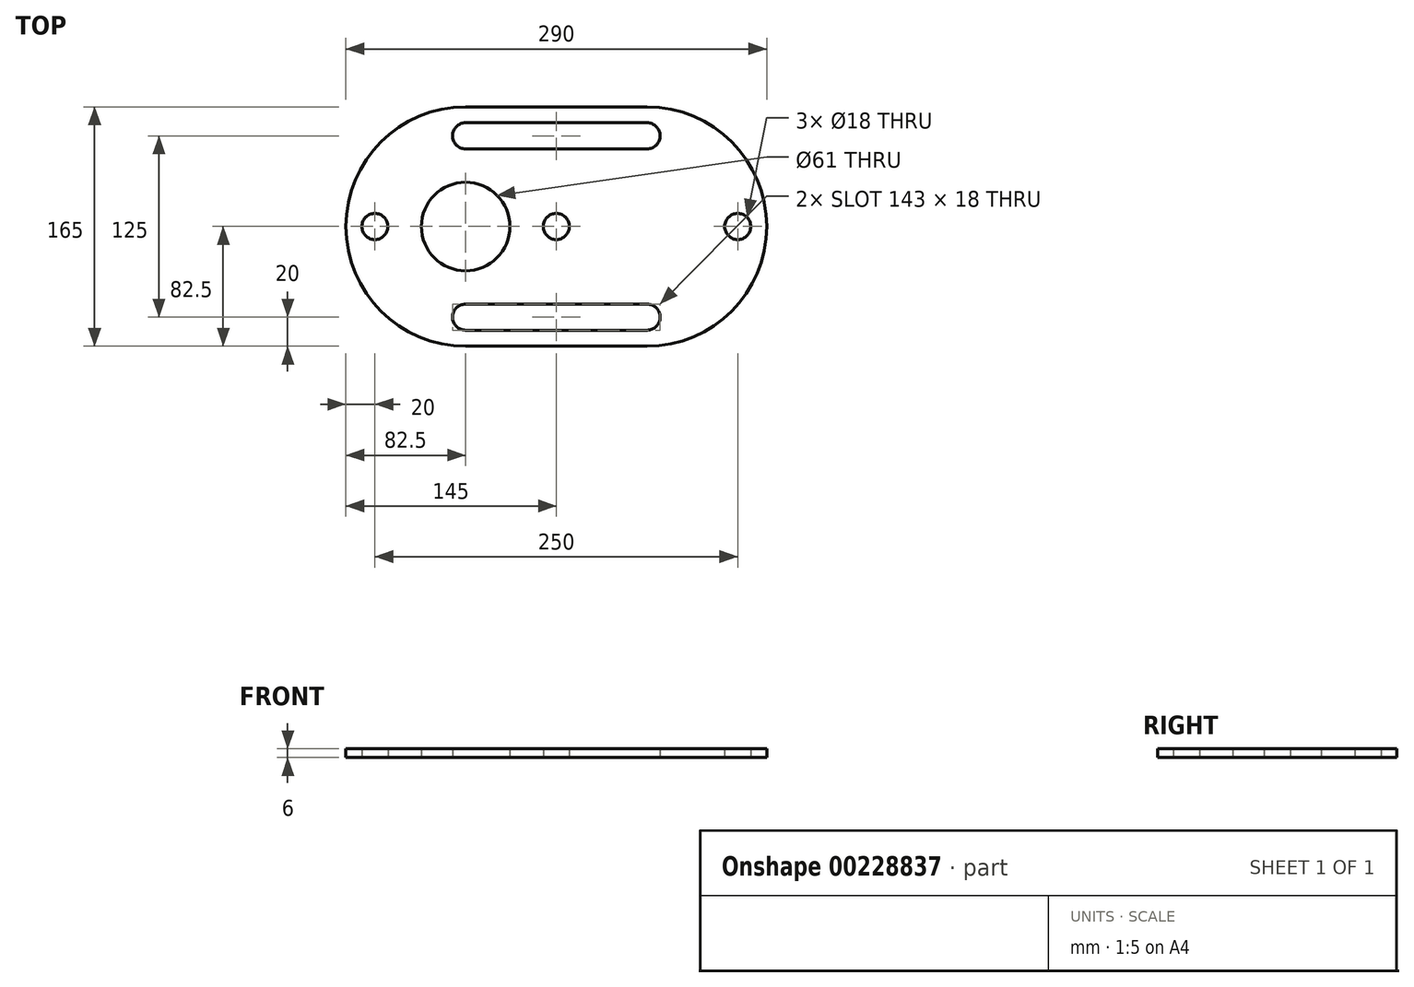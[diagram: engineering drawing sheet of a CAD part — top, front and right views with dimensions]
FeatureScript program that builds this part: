
annotation { "Feature Type Name" : "Feature", "Feature Type Description" : "" }
export const myFeature = defineFeature(function(context is Context, id is Id, definition is map)
    precondition{}
    {
        {
            var Q0;
            Q0=qCreatedBy(makeId("Top.planeOp"),FACE);
            var sketch = newSketch(context, id + "F0", { "sketchPlane" : qUnion([Q0])});
            skArc(sketch, "E0", {"start": v(-62.5, 82.5) * mm, "mid": v(-145, 0) * mm, "end": v(-62.5, -82.5) * mm});
            skLineSegment(sketch, "E1", {"start": v(-62.5, 82.5) * mm, "end": v(62.5, 82.5) * mm});
            skLineSegment(sketch, "E2", {"start": v(-62.5, -82.5) * mm, "end": v(62.5, -82.5) * mm});
            skArc(sketch, "E3.trimOffspring", {"start": v(62.5, -82.5) * mm, "mid": v(145, 0) * mm, "end": v(62.5, 82.5) * mm});
            skPoint(sketch, "E4.end.orphan", {"position": v(50.96, 0) * mm});
            skCircle(sketch, "E5", {"center": v(-62.5, 0) * mm, "radius": 30.5 * mm});
            skCircle(sketch, "E6", {"center": v(-62.5, 0) * mm, "radius": 62.5 * mm, "construction": true});
            skLineSegment(sketch, "E7", {"start": v(-62.5, 0) * mm, "end": v(62.5, 0) * mm, "construction": true});
            skCircle(sketch, "E8.MirrorC", {"center": v(62.5, 0) * mm, "radius": 62.5 * mm, "construction": true});
            skCircle(sketch, "E9", {"center": v(-125, 0) * mm, "radius": 9 * mm});
            skCircle(sketch, "E10", {"center": v(125, 0) * mm, "radius": 9 * mm});
            skArc(sketch, "E11", {"start": v(-62.5, -53.5) * mm, "mid": v(-71.5, -62.5) * mm, "end": v(-62.5, -71.5) * mm});
            skArc(sketch, "E12", {"start": v(62.5, -71.5) * mm, "mid": v(71.5, -62.5) * mm, "end": v(62.5, -53.5) * mm});
            skLineSegment(sketch, "E13", {"start": v(-62.5, -53.5) * mm, "end": v(62.5, -53.5) * mm});
            skLineSegment(sketch, "E14", {"start": v(62.5, -71.5) * mm, "end": v(-62.5, -71.5) * mm});
            skArc(sketch, "E15.MirrorCS", {"start": v(-62.5, 53.5) * mm, "mid": v(-71.5, 62.5) * mm, "end": v(-62.5, 71.5) * mm});
            skArc(sketch, "E16.MirrorCS", {"start": v(62.5, 71.5) * mm, "mid": v(71.5, 62.5) * mm, "end": v(62.5, 53.5) * mm});
            skLineSegment(sketch, "E17.MirrorCS", {"start": v(62.5, 71.5) * mm, "end": v(-62.5, 71.5) * mm});
            skLineSegment(sketch, "E18.MirrorCS", {"start": v(-62.5, 53.5) * mm, "end": v(62.5, 53.5) * mm});
            skCircle(sketch, "E19", {"center": v(0, 0) * mm, "radius": 9 * mm});
            skSolve(sketch);
        }
        {
            var Q0;
            Q0 = qSketchRegion(id + "F0", true);
            extrude(context, id + "F1", {"entities" : qUnion([Q0]), "flatOperationType" : FlatOperationType.REMOVE, "offsetDistance" : 25 * mm, "depth" : 6 * mm, "domain" : OperationDomain.MODEL});
        }
    });
